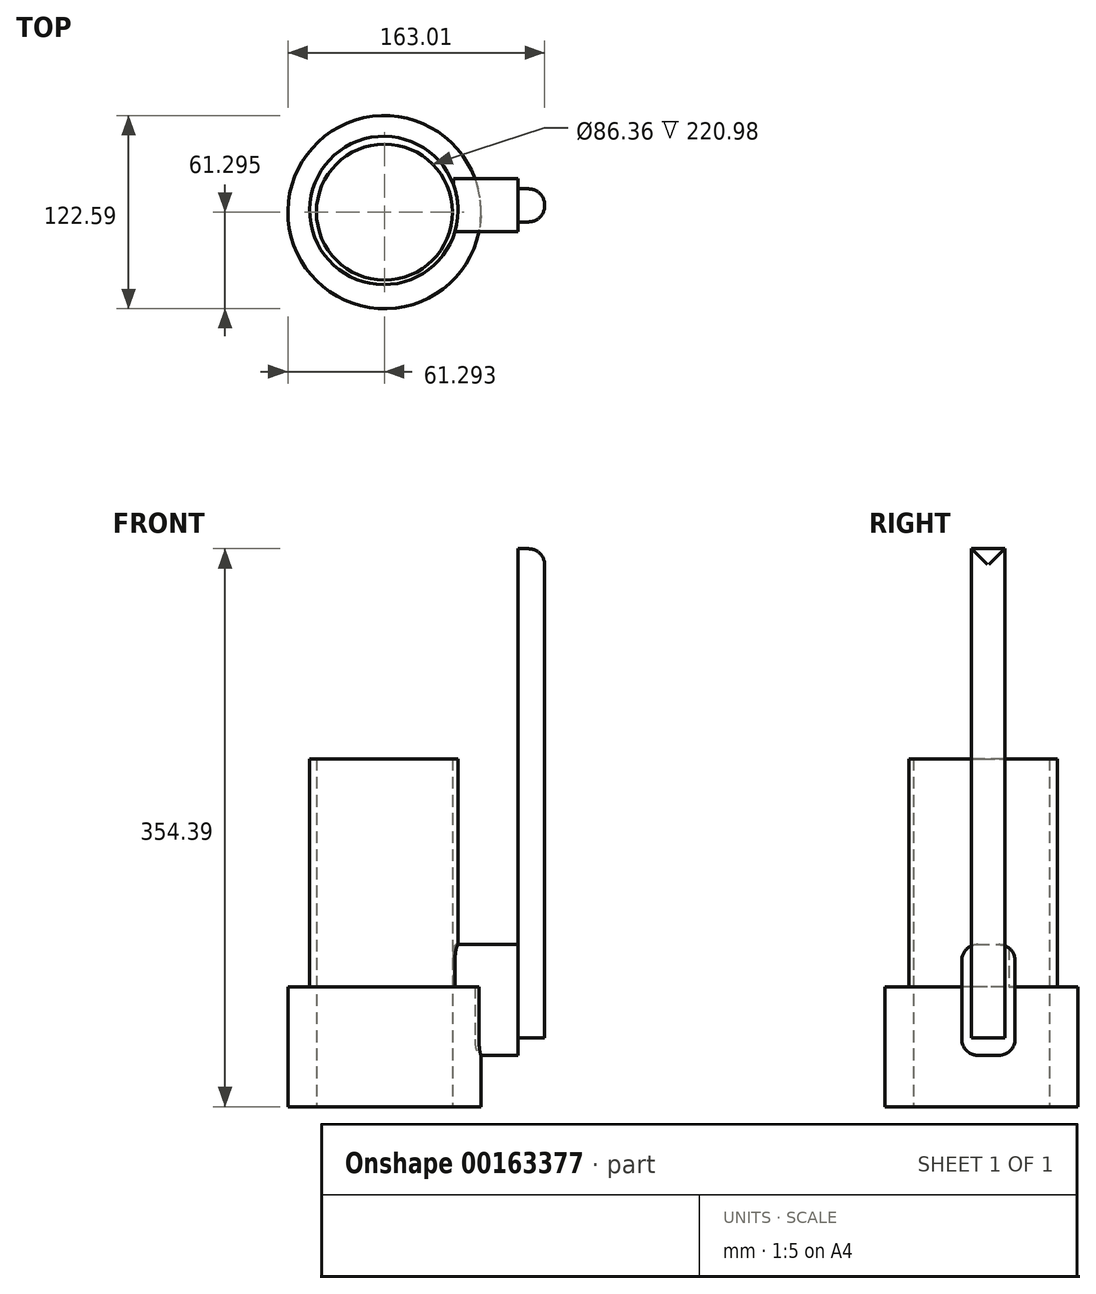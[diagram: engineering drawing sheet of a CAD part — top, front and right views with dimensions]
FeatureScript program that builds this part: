
annotation { "Feature Type Name" : "Feature", "Feature Type Description" : "" }
export const myFeature = defineFeature(function(context is Context, id is Id, definition is map)
    precondition{}
    {
        {
            var Q0;
            Q0=qCreatedBy(makeId("Top.planeOp"),FACE);
            var sketch = newSketch(context, id + "F0", { "sketchPlane" : qUnion([Q0])});
            skCircle(sketch, "E0", {"center": v(-44.17, -30.72) * mm, "radius": 47.12 * mm});
            skSolve(sketch);
        }
        {
            var Q0;
            Q0=makeQuery(id+"F0.imprint","IMPRINT",FACE,{"disambiguationData":[TD([[makeQuery(id+"F0.imprint","IMPRINT",EDGE,{"derivedFrom":sQuery(id+"F0.wireOp",EDGE,"E0")}),1.0]])]});
            extrude(context, id + "F1", {"entities" : qUnion([Q0]), "depth" : 220.98 * mm});
        }
        {
            var Q0;
            Q0=makeQuery(id+"F1.opExtrude","CAP_FACE",FACE,{"disambiguationData":[OSD([sQuery(id+"F0.wireOp",EDGE,"E0")])],"isStart":true});
            var sketch = newSketch(context, id + "F2", { "sketchPlane" : qUnion([Q0])});
            skPoint(sketch, "E1", {"position": v(-44.17, 30.72) * mm});
            skSolve(sketch);
        }
        {
            var Q0;
            Q0=sQuery(id+"F2.wireOp",VERTEX,"E1");
            var Q1;
            Q1=makeQuery(id+"F1.opExtrude","SWEPT_BODY",BODY,{"disambiguationData":[OSD([sQuery(id+"F0.wireOp",EDGE,"E0")])]});
            hole(context, id + "F3", {"style" : HoleStyle.SIMPLE, "endStyle" : HoleEndStyle.THROUGH, "holeDiameter" : 78.74 * mm, "locations" : qUnion([Q0]), "scope" : qUnion([Q1]), "isTappedThrough" : true});
        }
        {
            var Q0;
            Q0=qCreatedBy(makeId("Top.planeOp"),FACE);
            var sketch = newSketch(context, id + "F4", { "sketchPlane" : qUnion([Q0])});
            skCircle(sketch, "E2", {"center": v(-43.8, -31.8) * mm, "radius": 61.3 * mm});
            skSolve(sketch);
        }
        {
            var Q0;
            Q0=makeQuery(id+"F4.imprint","IMPRINT",FACE,{"disambiguationData":[TD([[makeQuery(id+"F4.imprint","IMPRINT",EDGE,{"derivedFrom":sQuery(id+"F4.wireOp",EDGE,"E2")}),1.0]])]});
            extrude(context, id + "F5", {"entities" : qUnion([Q0]), "operationType" : NewBodyOperationType.ADD, "depth" : 76.2 * mm});
        }
        {
            var Q0;
            Q0=makeQuery(id+"F5.boolean.opBoolean","MERGE",FACE,{"derivedFrom":[makeQuery(id+"F1.opExtrude","CAP_FACE",FACE,{"disambiguationData":[OSD([sQuery(id+"F0.wireOp",EDGE,"E0")])],"isStart":true}),makeQuery(id+"F5.opExtrude","CAP_FACE",FACE,{"disambiguationData":[OSD([sQuery(id+"F4.wireOp",EDGE,"E2")])],"isStart":true})]});
            var sketch = newSketch(context, id + "F6", { "sketchPlane" : qUnion([Q0])});
            skPoint(sketch, "E3", {"position": v(-43.8, 31.8) * mm});
            skSolve(sketch);
        }
        {
            var Q0;
            Q0=sQuery(id+"F6.wireOp",VERTEX,"E3");
            var Q1;
            Q1=makeQuery(id+"F1.opExtrude","SWEPT_BODY",BODY,{"disambiguationData":[OSD([sQuery(id+"F0.wireOp",EDGE,"E0")])]});
            hole(context, id + "F7", {"style" : HoleStyle.SIMPLE, "endStyle" : HoleEndStyle.THROUGH, "holeDiameter" : 86.36 * mm, "locations" : qUnion([Q0]), "scope" : qUnion([Q1]), "isTappedThrough" : true});
        }
        {
            var Q0;
            Q0=qCreatedBy(makeId("Right.planeOp"),FACE);
            var sketch = newSketch(context, id + "F8", { "sketchPlane" : qUnion([Q0])});
            skLineSegment(sketch, "E4.bottom", {"start": v(-44.25, 32.65) * mm, "end": v(-10.42, 32.65) * mm});
            skLineSegment(sketch, "E4.top", {"start": v(-44.25, 102.94) * mm, "end": v(-10.42, 102.94) * mm});
            skLineSegment(sketch, "E4.left", {"start": v(-44.25, 32.65) * mm, "end": v(-44.25, 102.94) * mm});
            skLineSegment(sketch, "E4.right", {"start": v(-10.42, 32.65) * mm, "end": v(-10.42, 102.94) * mm});
            skSolve(sketch);
        }
        {
            var Q0;
            Q0 = qSketchRegion(id + "F8", true);
            extrude(context, id + "F9", {"entities" : qUnion([Q0]), "operationType" : NewBodyOperationType.ADD, "depth" : 40.9 * mm});
        }
        {
            var Q0;
            Q0=makeQuery(id+"F9.opExtrude","SWEPT_EDGE",EDGE,{"disambiguationData":[OSD([sQuery(id+"F8.wireOp",EDGE,"E4.top"),sQuery(id+"F8.wireOp",EDGE,"E4.right")])]});
            var Q1;
            Q1=makeQuery(id+"F9.opExtrude","SWEPT_EDGE",EDGE,{"disambiguationData":[OSD([sQuery(id+"F8.wireOp",EDGE,"E4.top"),sQuery(id+"F8.wireOp",EDGE,"E4.left")])]});
            var Q2;
            Q2=makeQuery(id+"F9.opExtrude","SWEPT_EDGE",EDGE,{"disambiguationData":[OSD([sQuery(id+"F8.wireOp",EDGE,"E4.bottom"),sQuery(id+"F8.wireOp",EDGE,"E4.right")])]});
            var Q3;
            Q3=makeQuery(id+"F9.opExtrude","SWEPT_EDGE",EDGE,{"disambiguationData":[OSD([sQuery(id+"F8.wireOp",EDGE,"E4.bottom"),sQuery(id+"F8.wireOp",EDGE,"E4.left")])]});
            fillet(context, id + "F10", {"entities" : qUnion([Q0, Q1, Q2, Q3]), "radius" : 10.16 * mm, "tangentPropagation" : true, "allowEdgeOverflow" : false});
        }
        {
            var Q0;
            Q0=makeQuery(id+"F9.opExtrude","CAP_FACE",FACE,{"disambiguationData":[OSD([sQuery(id+"F8.wireOp",EDGE,"E4.bottom"),sQuery(id+"F8.wireOp",EDGE,"E4.top"),sQuery(id+"F8.wireOp",EDGE,"E4.left"),sQuery(id+"F8.wireOp",EDGE,"E4.right")])],"isStart":false});
            var sketch = newSketch(context, id + "F11", { "sketchPlane" : qUnion([Q0])});
            skLineSegment(sketch, "E5.bottom", {"start": v(-38.01, 45.78) * mm, "end": v(-17, 45.78) * mm});
            skLineSegment(sketch, "E5.top", {"start": v(-38.01, 43.81) * mm, "end": v(-17, 43.81) * mm});
            skLineSegment(sketch, "E5.left", {"start": v(-38.01, 45.78) * mm, "end": v(-38.01, 43.81) * mm});
            skLineSegment(sketch, "E5.right", {"start": v(-17, 45.78) * mm, "end": v(-17, 43.81) * mm});
            skSolve(sketch);
        }
        {
            var Q0;
            Q0 = qSketchRegion(id + "F11", true);
            extrude(context, id + "F12", {"entities" : qUnion([Q0]), "operationType" : NewBodyOperationType.ADD, "depth" : 17.02 * mm});
        }
        {
            var Q0;
            Q0=makeQuery(id+"F12.opExtrude","SWEPT_FACE",FACE,{"disambiguationData":[OSD([sQuery(id+"F11.wireOp",EDGE,"E5.bottom")])]});
            var sketch = newSketch(context, id + "F13", { "sketchPlane" : qUnion([Q0])});
            skLineSegment(sketch, "E6.bottom", {"start": v(40.9, -38.01) * mm, "end": v(60.17, -38.01) * mm});
            skLineSegment(sketch, "E6.top", {"start": v(40.9, -17) * mm, "end": v(60.17, -17) * mm});
            skLineSegment(sketch, "E6.left", {"start": v(40.9, -38.01) * mm, "end": v(40.9, -17) * mm});
            skLineSegment(sketch, "E6.right", {"start": v(60.17, -38.01) * mm, "end": v(60.17, -17) * mm});
            skSolve(sketch);
        }
        {
            var Q0;
            Q0=makeQuery(id+"F13.imprint","IMPRINT",FACE,{"disambiguationData":[TD([[makeQuery(id+"F13.imprint","IMPRINT",EDGE,{"derivedFrom":sQuery(id+"F13.wireOp",EDGE,"E6.bottom")}),-1.0]])]});
            extrude(context, id + "F14", {"entities" : qUnion([Q0]), "operationType" : NewBodyOperationType.ADD, "depth" : 308.6 * mm});
        }
        {
            var Q0;
            Q0=makeQuery(id+"F14.boolean.opBoolean","MERGE",EDGE,{"derivedFrom":[makeQuery(id+"F12.opExtrude","CAP_EDGE",EDGE,{"disambiguationData":[OSD([sQuery(id+"F11.wireOp",EDGE,"E5.left")])],"isStart":false}),makeQuery(id+"F14.opExtrude","SWEPT_EDGE",EDGE,{"disambiguationData":[OSD([sQuery(id+"F11.wireOp",EDGE,"E5.bottom"),sQuery(id+"F13.wireOp",EDGE,"E6.bottom")])]})]});
            var Q1;
            Q1=makeQuery(id+"F14.opExtrude","CAP_EDGE",EDGE,{"disambiguationData":[OSD([sQuery(id+"F11.wireOp",EDGE,"E5.bottom")])],"isStart":false});
            var Q2;
            Q2=makeQuery(id+"F14.boolean.opBoolean","MERGE",EDGE,{"derivedFrom":[makeQuery(id+"F12.opExtrude","CAP_EDGE",EDGE,{"disambiguationData":[OSD([sQuery(id+"F11.wireOp",EDGE,"E5.right")])],"isStart":false}),makeQuery(id+"F14.opExtrude","SWEPT_EDGE",EDGE,{"disambiguationData":[OSD([sQuery(id+"F11.wireOp",EDGE,"E5.bottom"),sQuery(id+"F13.wireOp",EDGE,"E6.top")])]})]});
            fillet(context, id + "F15", {"entities" : qUnion([Q0, Q1, Q2]), "radius" : 10.16 * mm, "tangentPropagation" : true, "allowEdgeOverflow" : false});
        }
    });
